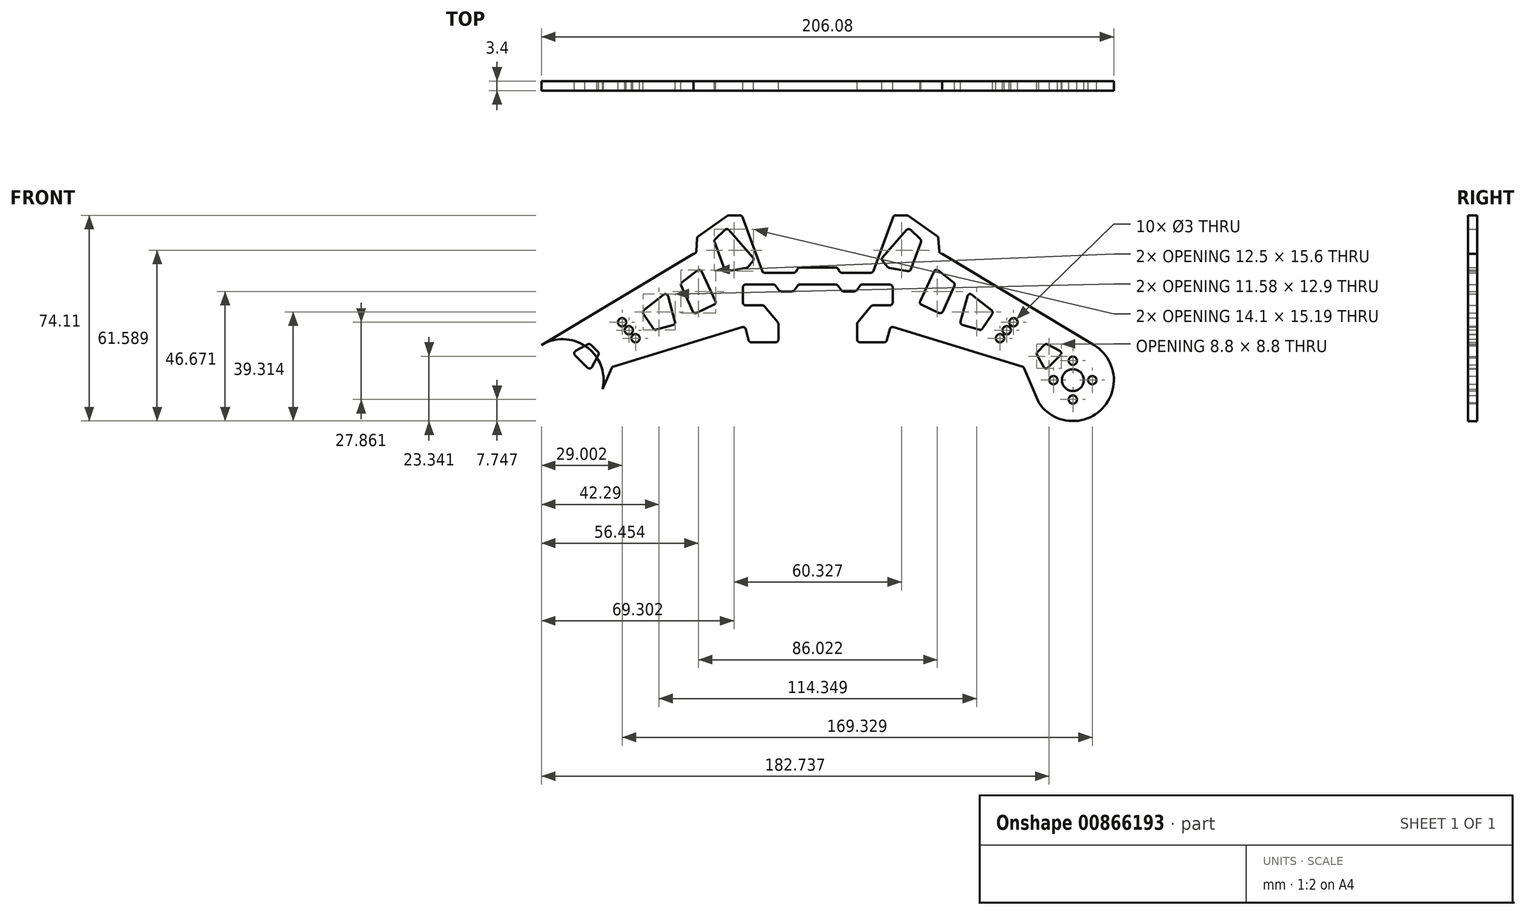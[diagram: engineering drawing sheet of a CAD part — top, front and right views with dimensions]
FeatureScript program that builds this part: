
annotation { "Feature Type Name" : "Feature", "Feature Type Description" : "" }
export const myFeature = defineFeature(function(context is Context, id is Id, definition is map)
    precondition{}
    {
        {
            var Q0;
            Q0=qCreatedBy(makeId("Front.planeOp"),FACE);
            var sketch = newSketch(context, id + "F0", { "sketchPlane" : qUnion([Q0])});
            skLineSegment(sketch, "E0", {"start": v(-61.8, 49.47) * mm, "end": v(-7.12, 16.59) * mm});
            skCircle(sketch, "E1", {"center": v(-14.72, 3.95) * mm, "radius": 14.75 * mm});
            skLineSegment(sketch, "E2", {"start": v(-32.97, 8.88) * mm, "end": v(-79.35, 23.06) * mm});
            skLineSegment(sketch, "E3", {"start": v(-62.84, 50.4) * mm, "end": v(-63.17, 55.1) * mm});
            skLineSegment(sketch, "E4", {"start": v(-63.6, 55.84) * mm, "end": v(-74, 63.13) * mm});
            skLineSegment(sketch, "E5", {"start": v(-74.58, 63.31) * mm, "end": v(-78.56, 63.31) * mm});
            skLineSegment(sketch, "E6", {"start": v(-79.5, 62.65) * mm, "end": v(-86.55, 43.3) * mm});
            skLineSegment(sketch, "E7", {"start": v(-87.49, 42.64) * mm, "end": v(-97.91, 42.64) * mm});
            skLineSegment(sketch, "E8", {"start": v(-98.78, 43.14) * mm, "end": v(-99.3, 44.04) * mm});
            skLineSegment(sketch, "E9", {"start": v(-100.16, 44.54) * mm, "end": v(-106.59, 44.54) * mm});
            skLineSegment(sketch, "E10", {"start": v(-80.6, 22.36) * mm, "end": v(-81.7, 18.31) * mm});
            skLineSegment(sketch, "E11", {"start": v(-82.66, 17.57) * mm, "end": v(-91.4, 17.57) * mm});
            skLineSegment(sketch, "E12", {"start": v(-92.4, 18.57) * mm, "end": v(-92.4, 24.2) * mm});
            skLineSegment(sketch, "E13", {"start": v(-92.16, 24.85) * mm, "end": v(-87.39, 30.53) * mm});
            skLineSegment(sketch, "E14", {"start": v(-86.62, 30.89) * mm, "end": v(-80.62, 30.89) * mm});
            skLineSegment(sketch, "E15", {"start": v(-79.62, 31.89) * mm, "end": v(-79.62, 37.39) * mm});
            skLineSegment(sketch, "E16", {"start": v(-80.62, 38.39) * mm, "end": v(-90.62, 38.39) * mm});
            skLineSegment(sketch, "E17", {"start": v(-91.44, 37.96) * mm, "end": v(-92.57, 36.36) * mm});
            skLineSegment(sketch, "E18", {"start": v(-93.39, 35.93) * mm, "end": v(-97.34, 35.93) * mm});
            skLineSegment(sketch, "E19", {"start": v(-98.16, 36.36) * mm, "end": v(-99.29, 37.96) * mm});
            skLineSegment(sketch, "E20", {"start": v(-100.1, 38.39) * mm, "end": v(-106.59, 38.39) * mm});
            skLineSegment(sketch, "E21", {"start": v(-32.34, 8.32) * mm, "end": v(-27.05, -4.14) * mm});
            skCircle(sketch, "E22", {"center": v(-14.72, 3.95) * mm, "radius": 3.93 * mm});
            skLineSegment(sketch, "E23", {"start": v(-14.72, 3.95) * mm, "end": v(-14.72, 10.95) * mm, "construction": true});
            skLineSegment(sketch, "E24", {"start": v(-14.72, 3.95) * mm, "end": v(-7.72, 3.95) * mm, "construction": true});
            skLineSegment(sketch, "E25", {"start": v(-14.72, 3.95) * mm, "end": v(-21.72, 3.95) * mm, "construction": true});
            skLineSegment(sketch, "E26", {"start": v(-14.72, 3.95) * mm, "end": v(-14.72, -3.05) * mm, "construction": true});
            skCircle(sketch, "E27", {"center": v(-14.72, -3.05) * mm, "radius": 1.5 * mm});
            skCircle(sketch, "E28", {"center": v(-7.72, 3.95) * mm, "radius": 1.5 * mm});
            skCircle(sketch, "E29", {"center": v(-14.72, 10.95) * mm, "radius": 1.5 * mm});
            skCircle(sketch, "E30", {"center": v(-21.72, 3.95) * mm, "radius": 1.5 * mm});
            skLineSegment(sketch, "E31", {"start": v(-23.67, 8.43) * mm, "end": v(-19.2, 12.9) * mm});
            skLineSegment(sketch, "E32", {"start": v(-19.43, 14.48) * mm, "end": v(-23.76, 16.82) * mm});
            skLineSegment(sketch, "E33", {"start": v(-24.94, 16.65) * mm, "end": v(-27.42, 14.17) * mm});
            skLineSegment(sketch, "E34", {"start": v(-27.6, 12.98) * mm, "end": v(-25.26, 8.66) * mm});
            skPoint(sketch, "E35", {"position": v(-21.44, 10.66) * mm});
            skCircle(sketch, "E36", {"center": v(-40.97, 19.03) * mm, "radius": 1.5 * mm});
            skCircle(sketch, "E37", {"center": v(-38.55, 21.92) * mm, "radius": 1.5 * mm});
            skCircle(sketch, "E38", {"center": v(-36.12, 24.8) * mm, "radius": 1.5 * mm});
            skLineSegment(sketch, "E39", {"start": v(-38.55, 21.92) * mm, "end": v(-40.97, 19.03) * mm, "construction": true});
            skLineSegment(sketch, "E40", {"start": v(-36.12, 24.8) * mm, "end": v(-38.55, 21.92) * mm, "construction": true});
            skLineSegment(sketch, "E41", {"start": v(-47.33, 22.5) * mm, "end": v(-43.8, 27.78) * mm});
            skLineSegment(sketch, "E42", {"start": v(-44, 29.12) * mm, "end": v(-51.1, 34.75) * mm});
            skLineSegment(sketch, "E43", {"start": v(-52.69, 34.23) * mm, "end": v(-55.17, 25.06) * mm});
            skLineSegment(sketch, "E44", {"start": v(-54.48, 23.84) * mm, "end": v(-48.43, 22.1) * mm});
            skPoint(sketch, "E45", {"position": v(-45.5, 25.23) * mm});
            skPoint(sketch, "E46.endSnap0", {"position": v(-56.43, 16.06) * mm});
            skLineSegment(sketch, "E47", {"start": v(-62.92, 28.16) * mm, "end": v(-69.25, 31.12) * mm});
            skLineSegment(sketch, "E48", {"start": v(-69.73, 32.45) * mm, "end": v(-64.77, 43.1) * mm});
            skLineSegment(sketch, "E49", {"start": v(-63.25, 43.46) * mm, "end": v(-57.7, 39.17) * mm});
            skLineSegment(sketch, "E50", {"start": v(-57.41, 37.97) * mm, "end": v(-61.58, 28.66) * mm});
            skPoint(sketch, "E51.visualSharp", {"position": v(-64.24, 44.23) * mm});
            skArc(sketch, "E51.filletArc", {"start": v(-63.25, 43.46) * mm, "mid": v(-64.1, 43.64) * mm, "end": v(-64.77, 43.1) * mm});
            skPoint(sketch, "E52.visualSharp", {"position": v(-57.09, 38.69) * mm});
            skArc(sketch, "E52.filletArc", {"start": v(-57.41, 37.97) * mm, "mid": v(-57.35, 38.62) * mm, "end": v(-57.7, 39.17) * mm});
            skPoint(sketch, "E53.visualSharp", {"position": v(-70.15, 31.54) * mm});
            skArc(sketch, "E53.filletArc", {"start": v(-69.73, 32.45) * mm, "mid": v(-69.76, 31.68) * mm, "end": v(-69.25, 31.12) * mm});
            skPoint(sketch, "E54.visualSharp", {"position": v(-62, 27.74) * mm});
            skArc(sketch, "E54.filletArc", {"start": v(-62.92, 28.16) * mm, "mid": v(-62.14, 28.13) * mm, "end": v(-61.58, 28.66) * mm});
            skPoint(sketch, "E55.visualSharp", {"position": v(-52.29, 35.7) * mm});
            skArc(sketch, "E55.filletArc", {"start": v(-51.1, 34.75) * mm, "mid": v(-52.03, 34.91) * mm, "end": v(-52.69, 34.23) * mm});
            skPoint(sketch, "E56.visualSharp", {"position": v(-43.28, 28.55) * mm});
            skArc(sketch, "E56.filletArc", {"start": v(-43.8, 27.78) * mm, "mid": v(-43.63, 28.5) * mm, "end": v(-44, 29.12) * mm});
            skPoint(sketch, "E57.visualSharp", {"position": v(-55.42, 24.1) * mm});
            skArc(sketch, "E57.filletArc", {"start": v(-55.17, 25.06) * mm, "mid": v(-55.07, 24.3) * mm, "end": v(-54.48, 23.84) * mm});
            skPoint(sketch, "E58.visualSharp", {"position": v(-47.73, 21.9) * mm});
            skArc(sketch, "E58.filletArc", {"start": v(-48.43, 22.1) * mm, "mid": v(-47.81, 22.13) * mm, "end": v(-47.33, 22.5) * mm});
            skPoint(sketch, "E59.visualSharp", {"position": v(-27.95, 13.64) * mm});
            skArc(sketch, "E59.filletArc", {"start": v(-27.42, 14.17) * mm, "mid": v(-27.7, 13.6) * mm, "end": v(-27.6, 12.98) * mm});
            skPoint(sketch, "E60.visualSharp", {"position": v(-24.41, 17.18) * mm});
            skArc(sketch, "E60.filletArc", {"start": v(-23.76, 16.82) * mm, "mid": v(-24.38, 16.93) * mm, "end": v(-24.94, 16.65) * mm});
            skPoint(sketch, "E61.visualSharp", {"position": v(-24.62, 7.48) * mm});
            skArc(sketch, "E61.filletArc", {"start": v(-25.26, 8.66) * mm, "mid": v(-24.52, 8.15) * mm, "end": v(-23.67, 8.43) * mm});
            skPoint(sketch, "E62.visualSharp", {"position": v(-18.25, 13.85) * mm});
            skArc(sketch, "E62.filletArc", {"start": v(-19.2, 12.9) * mm, "mid": v(-18.92, 13.75) * mm, "end": v(-19.43, 14.48) * mm});
            skPoint(sketch, "E63.visualSharp", {"position": v(-62.82, 50.08) * mm});
            skArc(sketch, "E63.filletArc", {"start": v(-62.84, 50.4) * mm, "mid": v(-62.51, 49.72) * mm, "end": v(-61.8, 49.47) * mm});
            skPoint(sketch, "E64.visualSharp", {"position": v(-63.2, 55.57) * mm});
            skArc(sketch, "E64.filletArc", {"start": v(-63.17, 55.1) * mm, "mid": v(-63.3, 55.52) * mm, "end": v(-63.6, 55.84) * mm});
            skPoint(sketch, "E65.visualSharp", {"position": v(-99.59, 38.39) * mm});
            skArc(sketch, "E65.filletArc", {"start": v(-99.29, 37.96) * mm, "mid": v(-99.64, 38.28) * mm, "end": v(-100.1, 38.39) * mm});
            skPoint(sketch, "E66.visualSharp", {"position": v(-97.86, 35.93) * mm});
            skArc(sketch, "E66.filletArc", {"start": v(-98.16, 36.36) * mm, "mid": v(-97.8, 36.04) * mm, "end": v(-97.34, 35.93) * mm});
            skPoint(sketch, "E67.visualSharp", {"position": v(-92.86, 35.93) * mm});
            skArc(sketch, "E67.filletArc", {"start": v(-93.39, 35.93) * mm, "mid": v(-92.92, 36.04) * mm, "end": v(-92.57, 36.36) * mm});
            skPoint(sketch, "E68.visualSharp", {"position": v(-91.14, 38.39) * mm});
            skArc(sketch, "E68.filletArc", {"start": v(-90.62, 38.39) * mm, "mid": v(-91.08, 38.28) * mm, "end": v(-91.44, 37.96) * mm});
            skPoint(sketch, "E69.visualSharp", {"position": v(-79.62, 38.39) * mm});
            skArc(sketch, "E69.filletArc", {"start": v(-79.62, 37.39) * mm, "mid": v(-79.92, 38.1) * mm, "end": v(-80.62, 38.39) * mm});
            skPoint(sketch, "E70.visualSharp", {"position": v(-79.62, 30.89) * mm});
            skArc(sketch, "E70.filletArc", {"start": v(-80.62, 30.89) * mm, "mid": v(-79.92, 31.18) * mm, "end": v(-79.62, 31.89) * mm});
            skPoint(sketch, "E71.visualSharp", {"position": v(-87.09, 30.89) * mm});
            skArc(sketch, "E71.filletArc", {"start": v(-86.62, 30.89) * mm, "mid": v(-87.05, 30.8) * mm, "end": v(-87.39, 30.53) * mm});
            skPoint(sketch, "E72.visualSharp", {"position": v(-92.4, 24.57) * mm});
            skArc(sketch, "E72.filletArc", {"start": v(-92.16, 24.85) * mm, "mid": v(-92.33, 24.55) * mm, "end": v(-92.4, 24.2) * mm});
            skPoint(sketch, "E73.visualSharp", {"position": v(-92.4, 17.57) * mm});
            skArc(sketch, "E73.filletArc", {"start": v(-92.4, 18.57) * mm, "mid": v(-92.1, 17.86) * mm, "end": v(-91.4, 17.57) * mm});
            skPoint(sketch, "E74.visualSharp", {"position": v(-81.9, 17.57) * mm});
            skArc(sketch, "E74.filletArc", {"start": v(-82.66, 17.57) * mm, "mid": v(-82.05, 17.78) * mm, "end": v(-81.7, 18.31) * mm});
            skPoint(sketch, "E75.visualSharp", {"position": v(-80.34, 23.37) * mm});
            skArc(sketch, "E75.filletArc", {"start": v(-79.35, 23.06) * mm, "mid": v(-80.13, 22.98) * mm, "end": v(-80.6, 22.36) * mm});
            skPoint(sketch, "E76.visualSharp", {"position": v(-86.79, 42.64) * mm});
            skArc(sketch, "E76.filletArc", {"start": v(-87.49, 42.64) * mm, "mid": v(-86.91, 42.82) * mm, "end": v(-86.55, 43.3) * mm});
            skPoint(sketch, "E77.visualSharp", {"position": v(-32.52, 8.75) * mm});
            skArc(sketch, "E77.filletArc", {"start": v(-32.34, 8.32) * mm, "mid": v(-32.6, 8.67) * mm, "end": v(-32.97, 8.88) * mm});
            skPoint(sketch, "E78.visualSharp", {"position": v(-79.26, 63.31) * mm});
            skArc(sketch, "E78.filletArc", {"start": v(-78.56, 63.31) * mm, "mid": v(-79.14, 63.13) * mm, "end": v(-79.5, 62.65) * mm});
            skPoint(sketch, "E79.visualSharp", {"position": v(-74.26, 63.31) * mm});
            skArc(sketch, "E79.filletArc", {"start": v(-74, 63.13) * mm, "mid": v(-74.28, 63.27) * mm, "end": v(-74.58, 63.31) * mm});
            skLineSegment(sketch, "E80.MirrorCS", {"start": v(-74.58, 58.04) * mm, "end": v(-83.22, 48.2) * mm});
            skLineSegment(sketch, "E81.MirrorCS", {"start": v(-69.68, 54.77) * mm, "end": v(-73.13, 58.1) * mm});
            skLineSegment(sketch, "E82.MirrorCS", {"start": v(-80.87, 44.42) * mm, "end": v(-74.18, 43.21) * mm});
            skLineSegment(sketch, "E83.MirrorCS", {"start": v(-73.07, 43.85) * mm, "end": v(-69.43, 53.7) * mm});
            skLineSegment(sketch, "E84.MirrorCS", {"start": v(-83.24, 46.9) * mm, "end": v(-81.46, 44.77) * mm});
            skPoint(sketch, "E85.MirrorP", {"position": v(-86.1, 45.52) * mm});
            skPoint(sketch, "E86.visualSharp", {"position": v(-73.89, 58.83) * mm});
            skArc(sketch, "E86.filletArc", {"start": v(-73.13, 58.1) * mm, "mid": v(-73.87, 58.38) * mm, "end": v(-74.58, 58.04) * mm});
            skPoint(sketch, "E87.visualSharp", {"position": v(-69.2, 54.32) * mm});
            skArc(sketch, "E87.filletArc", {"start": v(-69.43, 53.7) * mm, "mid": v(-69.4, 54.28) * mm, "end": v(-69.68, 54.77) * mm});
            skPoint(sketch, "E88.visualSharp", {"position": v(-73.36, 43.06) * mm});
            skArc(sketch, "E88.filletArc", {"start": v(-74.18, 43.21) * mm, "mid": v(-73.5, 43.33) * mm, "end": v(-73.07, 43.85) * mm});
            skPoint(sketch, "E89.visualSharp", {"position": v(-81.23, 44.49) * mm});
            skArc(sketch, "E89.filletArc", {"start": v(-81.46, 44.77) * mm, "mid": v(-81.2, 44.54) * mm, "end": v(-80.87, 44.42) * mm});
            skPoint(sketch, "E90.visualSharp", {"position": v(-83.79, 47.56) * mm});
            skArc(sketch, "E90.filletArc", {"start": v(-83.22, 48.2) * mm, "mid": v(-83.47, 47.56) * mm, "end": v(-83.24, 46.9) * mm});
            skLineSegment(sketch, "E91", {"start": v(-36.12, 24.8) * mm, "end": v(-30.98, 30.94) * mm, "construction": true});
            skLineSegment(sketch, "E92", {"start": v(-40.97, 19.03) * mm, "end": v(-46.11, 12.9) * mm, "construction": true});
            skLineSegment(sketch, "E93", {"start": v(-14.72, 3.95) * mm, "end": v(-21.44, 10.66) * mm, "construction": true});
            skLineSegment(sketch, "E94", {"start": v(-47.73, 21.9) * mm, "end": v(-52.47, 14.84) * mm, "construction": true});
            skPoint(sketch, "E95.endSnap0", {"position": v(-34.46, 33.03) * mm});
            skLineSegment(sketch, "E96", {"start": v(-64.92, 29.1) * mm, "end": v(-68.24, 19.66) * mm, "construction": true});
            skLineSegment(sketch, "E97", {"start": v(-55.42, 24.1) * mm, "end": v(-57.6, 16.06) * mm, "construction": true});
            skLineSegment(sketch, "E98", {"start": v(-43.28, 28.55) * mm, "end": v(-38.6, 35.52) * mm, "construction": true});
            skLineSegment(sketch, "E99", {"start": v(-52.29, 35.7) * mm, "end": v(-50.41, 42.62) * mm, "construction": true});
            skPoint(sketch, "E100.visualSharp", {"position": v(-99.59, 44.54) * mm});
            skArc(sketch, "E100.filletArc", {"start": v(-99.3, 44.04) * mm, "mid": v(-99.66, 44.4) * mm, "end": v(-100.16, 44.54) * mm});
            skPoint(sketch, "E101.visualSharp", {"position": v(-98.49, 42.64) * mm});
            skArc(sketch, "E101.filletArc", {"start": v(-98.78, 43.14) * mm, "mid": v(-98.41, 42.77) * mm, "end": v(-97.91, 42.64) * mm});
            skLineSegment(sketch, "E102", {"start": v(-106.59, 44.54) * mm, "end": v(-106.59, 38.39) * mm, "construction": true});
            skArc(sketch, "E103.MirrorCS", {"start": v(-119.79, 35.93) * mm, "mid": v(-120.25, 36.04) * mm, "end": v(-120.6, 36.36) * mm});
            skArc(sketch, "E104.MirrorCS", {"start": v(-115, 36.36) * mm, "mid": v(-115.36, 36.04) * mm, "end": v(-115.83, 35.93) * mm});
            skLineSegment(sketch, "E105.MirrorCS", {"start": v(-121.73, 37.96) * mm, "end": v(-120.6, 36.36) * mm});
            skArc(sketch, "E106.MirrorCS", {"start": v(-122.55, 38.39) * mm, "mid": v(-122.09, 38.28) * mm, "end": v(-121.73, 37.96) * mm});
            skLineSegment(sketch, "E107.MirrorCS", {"start": v(-119.79, 35.93) * mm, "end": v(-115.83, 35.93) * mm});
            skArc(sketch, "E108.MirrorCS", {"start": v(-113.88, 37.96) * mm, "mid": v(-113.53, 38.28) * mm, "end": v(-113.06, 38.39) * mm});
            skLineSegment(sketch, "E109.MirrorCS", {"start": v(-115, 36.36) * mm, "end": v(-113.88, 37.96) * mm});
            skArc(sketch, "E110.MirrorCS", {"start": v(-131.7, 44.77) * mm, "mid": v(-131.97, 44.54) * mm, "end": v(-132.3, 44.42) * mm});
            skArc(sketch, "E111.MirrorCS", {"start": v(-180.83, 8.32) * mm, "mid": v(-180.58, 8.67) * mm, "end": v(-180.2, 8.88) * mm});
            skArc(sketch, "E112.MirrorCS", {"start": v(-113.87, 44.04) * mm, "mid": v(-113.5, 44.4) * mm, "end": v(-113, 44.54) * mm});
            skArc(sketch, "E113.MirrorCS", {"start": v(-164.74, 22.1) * mm, "mid": v(-165.36, 22.13) * mm, "end": v(-165.84, 22.5) * mm});
            skLineSegment(sketch, "E114.MirrorCS", {"start": v(-114.4, 43.14) * mm, "end": v(-113.87, 44.04) * mm});
            skArc(sketch, "E115.MirrorCS", {"start": v(-114.4, 43.14) * mm, "mid": v(-114.76, 42.77) * mm, "end": v(-115.26, 42.64) * mm});
            skArc(sketch, "E116.MirrorCS", {"start": v(-150.33, 50.4) * mm, "mid": v(-150.66, 49.72) * mm, "end": v(-151.37, 49.47) * mm});
            skArc(sketch, "E117.MirrorCS", {"start": v(-133.82, 23.06) * mm, "mid": v(-133.04, 22.98) * mm, "end": v(-132.56, 22.36) * mm});
            skArc(sketch, "E118.MirrorCS", {"start": v(-129.95, 48.2) * mm, "mid": v(-129.7, 47.56) * mm, "end": v(-129.93, 46.9) * mm});
            skArc(sketch, "E119.MirrorCS", {"start": v(-132.55, 30.89) * mm, "mid": v(-133.25, 31.18) * mm, "end": v(-133.55, 31.89) * mm});
            skArc(sketch, "E120.MirrorCS", {"start": v(-120.78, 18.57) * mm, "mid": v(-121.07, 17.86) * mm, "end": v(-121.78, 17.57) * mm});
            skLineSegment(sketch, "E121.MirrorCS", {"start": v(-129.93, 46.9) * mm, "end": v(-131.7, 44.77) * mm});
            skArc(sketch, "E122.MirrorCS", {"start": v(-149.92, 43.46) * mm, "mid": v(-149.08, 43.64) * mm, "end": v(-148.4, 43.1) * mm});
            skArc(sketch, "E123.MirrorCS", {"start": v(-133.55, 37.39) * mm, "mid": v(-133.25, 38.1) * mm, "end": v(-132.55, 38.39) * mm});
            skArc(sketch, "E124.MirrorCS", {"start": v(-121.01, 24.85) * mm, "mid": v(-120.84, 24.55) * mm, "end": v(-120.78, 24.2) * mm});
            skArc(sketch, "E125.MirrorCS", {"start": v(-143.74, 53.7) * mm, "mid": v(-143.78, 54.28) * mm, "end": v(-143.5, 54.77) * mm});
            skArc(sketch, "E126.MirrorCS", {"start": v(-126.55, 30.89) * mm, "mid": v(-126.12, 30.8) * mm, "end": v(-125.78, 30.53) * mm});
            skLineSegment(sketch, "E127.MirrorCS", {"start": v(-150.33, 50.4) * mm, "end": v(-150, 55.1) * mm});
            skLineSegment(sketch, "E128.MirrorCS", {"start": v(-133.55, 31.89) * mm, "end": v(-133.55, 37.39) * mm});
            skLineSegment(sketch, "E129.MirrorCS", {"start": v(-143.5, 54.77) * mm, "end": v(-140.04, 58.1) * mm});
            skArc(sketch, "E130.MirrorCS", {"start": v(-150, 55.1) * mm, "mid": v(-149.87, 55.52) * mm, "end": v(-149.57, 55.84) * mm});
            skArc(sketch, "E131.MirrorCS", {"start": v(-125.68, 42.64) * mm, "mid": v(-126.26, 42.82) * mm, "end": v(-126.62, 43.3) * mm});
            skLineSegment(sketch, "E132.MirrorCS", {"start": v(-120.78, 18.57) * mm, "end": v(-120.78, 24.2) * mm});
            skLineSegment(sketch, "E133.MirrorCS", {"start": v(-165.84, 22.5) * mm, "end": v(-169.38, 27.78) * mm});
            skArc(sketch, "E134.MirrorCS", {"start": v(-134.6, 63.31) * mm, "mid": v(-134.03, 63.13) * mm, "end": v(-133.67, 62.65) * mm});
            skLineSegment(sketch, "E135.MirrorCS", {"start": v(-138.6, 63.31) * mm, "end": v(-134.6, 63.31) * mm});
            skLineSegment(sketch, "E136.MirrorCS", {"start": v(-121.01, 24.85) * mm, "end": v(-125.78, 30.53) * mm});
            skLineSegment(sketch, "E137.MirrorCS", {"start": v(-132.3, 44.42) * mm, "end": v(-138.99, 43.21) * mm});
            skLineSegment(sketch, "E138.MirrorCS", {"start": v(-126.55, 30.89) * mm, "end": v(-132.55, 30.89) * mm});
            skArc(sketch, "E139.MirrorCS", {"start": v(-139.17, 63.13) * mm, "mid": v(-138.9, 63.27) * mm, "end": v(-138.6, 63.31) * mm});
            skArc(sketch, "E140.MirrorCS", {"start": v(-140.04, 58.1) * mm, "mid": v(-139.3, 58.38) * mm, "end": v(-138.6, 58.04) * mm});
            skArc(sketch, "E141.MirrorCS", {"start": v(-138.99, 43.21) * mm, "mid": v(-139.66, 43.33) * mm, "end": v(-140.1, 43.85) * mm});
            skArc(sketch, "E142.MirrorCS", {"start": v(-169.38, 27.78) * mm, "mid": v(-169.54, 28.5) * mm, "end": v(-169.17, 29.12) * mm});
            skLineSegment(sketch, "E143.MirrorCS", {"start": v(-158.7, 23.84) * mm, "end": v(-164.74, 22.1) * mm});
            skLineSegment(sketch, "E144.MirrorCS", {"start": v(-149.92, 43.46) * mm, "end": v(-155.46, 39.17) * mm});
            skArc(sketch, "E145.MirrorCS", {"start": v(-158, 25.06) * mm, "mid": v(-158.1, 24.3) * mm, "end": v(-158.7, 23.84) * mm});
            skArc(sketch, "E146.MirrorCS", {"start": v(-162.07, 34.75) * mm, "mid": v(-161.14, 34.91) * mm, "end": v(-160.49, 34.23) * mm});
            skArc(sketch, "E147.MirrorCS", {"start": v(-155.76, 37.97) * mm, "mid": v(-155.82, 38.62) * mm, "end": v(-155.46, 39.17) * mm});
            skArc(sketch, "E148.MirrorCS", {"start": v(-143.44, 32.45) * mm, "mid": v(-143.4, 31.68) * mm, "end": v(-143.92, 31.12) * mm});
            skLineSegment(sketch, "E149.MirrorCS", {"start": v(-188.23, 16.65) * mm, "end": v(-185.75, 14.17) * mm});
            skArc(sketch, "E150.MirrorCS", {"start": v(-130.51, 17.57) * mm, "mid": v(-131.12, 17.78) * mm, "end": v(-131.48, 18.31) * mm});
            skLineSegment(sketch, "E151.MirrorCS", {"start": v(-193.74, 14.48) * mm, "end": v(-189.41, 16.82) * mm});
            skLineSegment(sketch, "E152.MirrorCS", {"start": v(-132.56, 22.36) * mm, "end": v(-131.48, 18.31) * mm});
            skLineSegment(sketch, "E153.MirrorCS", {"start": v(-174.62, 21.92) * mm, "end": v(-172.2, 19.03) * mm, "construction": true});
            skLineSegment(sketch, "E154.MirrorCS", {"start": v(-150.25, 28.16) * mm, "end": v(-143.92, 31.12) * mm});
            skArc(sketch, "E155.MirrorCS", {"start": v(-187.91, 8.66) * mm, "mid": v(-188.65, 8.15) * mm, "end": v(-189.5, 8.43) * mm});
            skLineSegment(sketch, "E156.MirrorCS", {"start": v(-169.17, 29.12) * mm, "end": v(-162.07, 34.75) * mm});
            skLineSegment(sketch, "E157.MirrorCS", {"start": v(-185.58, 12.98) * mm, "end": v(-187.91, 8.66) * mm});
            skLineSegment(sketch, "E158.MirrorCS", {"start": v(-177.05, 24.8) * mm, "end": v(-174.62, 21.92) * mm, "construction": true});
            skCircle(sketch, "E159.MirrorC", {"center": v(-177.05, 24.8) * mm, "radius": 1.5 * mm});
            skArc(sketch, "E160.MirrorCS", {"start": v(-189.41, 16.82) * mm, "mid": v(-188.8, 16.93) * mm, "end": v(-188.23, 16.65) * mm});
            skCircle(sketch, "E161.MirrorC", {"center": v(-174.62, 21.92) * mm, "radius": 1.5 * mm});
            skCircle(sketch, "E162.MirrorC", {"center": v(-172.2, 19.03) * mm, "radius": 1.5 * mm});
            skLineSegment(sketch, "E163.MirrorCS", {"start": v(-189.5, 8.43) * mm, "end": v(-193.97, 12.9) * mm});
            skArc(sketch, "E164.MirrorCS", {"start": v(-193.97, 12.9) * mm, "mid": v(-194.25, 13.75) * mm, "end": v(-193.74, 14.48) * mm});
            skArc(sketch, "E165.MirrorCS", {"start": v(-185.75, 14.17) * mm, "mid": v(-185.47, 13.6) * mm, "end": v(-185.58, 12.98) * mm});
            skArc(sketch, "E166.MirrorCS", {"start": v(-150.25, 28.16) * mm, "mid": v(-151.03, 28.13) * mm, "end": v(-151.59, 28.66) * mm});
            skCircle(sketch, "E167.MirrorC", {"center": v(-191.45, 3.95) * mm, "radius": 1.5 * mm});
            skLineSegment(sketch, "E168.MirrorCS", {"start": v(-198.45, 3.95) * mm, "end": v(-191.45, 3.95) * mm, "construction": true});
            skLineSegment(sketch, "E169.MirrorCS", {"start": v(-198.45, 3.95) * mm, "end": v(-191.73, 10.66) * mm, "construction": true});
            skLineSegment(sketch, "E170.MirrorCS", {"start": v(-113, 44.54) * mm, "end": v(-106.59, 44.54) * mm});
            skLineSegment(sketch, "E171.MirrorCS", {"start": v(-198.45, 3.95) * mm, "end": v(-198.45, 10.95) * mm, "construction": true});
            skLineSegment(sketch, "E172.MirrorCS", {"start": v(-113.06, 38.39) * mm, "end": v(-106.59, 38.39) * mm});
            skLineSegment(sketch, "E173.MirrorCS", {"start": v(-149.57, 55.84) * mm, "end": v(-139.17, 63.13) * mm});
            skLineSegment(sketch, "E174.MirrorCS", {"start": v(-198.45, 3.95) * mm, "end": v(-205.45, 3.95) * mm, "construction": true});
            skCircle(sketch, "E175.MirrorC", {"center": v(-198.45, 3.95) * mm, "radius": 3.93 * mm});
            skLineSegment(sketch, "E176.MirrorCS", {"start": v(-198.45, 3.95) * mm, "end": v(-198.45, -3.05) * mm, "construction": true});
            skLineSegment(sketch, "E177.MirrorCS", {"start": v(-157.75, 24.1) * mm, "end": v(-155.57, 16.06) * mm, "construction": true});
            skCircle(sketch, "E178.MirrorC", {"center": v(-198.45, 10.95) * mm, "radius": 1.5 * mm});
            skCircle(sketch, "E179.MirrorC", {"center": v(-198.45, -3.05) * mm, "radius": 1.5 * mm});
            skCircle(sketch, "E180.MirrorC", {"center": v(-205.45, 3.95) * mm, "radius": 1.5 * mm});
            skPoint(sketch, "E181.MirrorP", {"position": v(-139.81, 43.06) * mm});
            skPoint(sketch, "E182.MirrorP", {"position": v(-133.55, 30.89) * mm});
            skLineSegment(sketch, "E183.MirrorCS", {"start": v(-125.68, 42.64) * mm, "end": v(-115.26, 42.64) * mm});
            skPoint(sketch, "E184.MirrorP", {"position": v(-129.38, 47.56) * mm});
            skLineSegment(sketch, "E185.MirrorCS", {"start": v(-155.76, 37.97) * mm, "end": v(-151.59, 28.66) * mm});
            skPoint(sketch, "E186.MirrorP", {"position": v(-114.68, 42.64) * mm});
            skPoint(sketch, "E187.MirrorP", {"position": v(-115.3, 35.93) * mm});
            skLineSegment(sketch, "E188.MirrorCS", {"start": v(-172.2, 19.03) * mm, "end": v(-167.06, 12.9) * mm, "construction": true});
            skLineSegment(sketch, "E189.MirrorCS", {"start": v(-180.83, 8.32) * mm, "end": v(-186.12, -4.14) * mm});
            skLineSegment(sketch, "E190.MirrorCS", {"start": v(-143.44, 32.45) * mm, "end": v(-148.4, 43.1) * mm});
            skPoint(sketch, "E191.MirrorP", {"position": v(-148.93, 44.23) * mm});
            skLineSegment(sketch, "E192.MirrorCS", {"start": v(-180.2, 8.88) * mm, "end": v(-133.82, 23.06) * mm});
            skLineSegment(sketch, "E193.MirrorCS", {"start": v(-138.6, 58.04) * mm, "end": v(-129.95, 48.2) * mm});
            skPoint(sketch, "E194.MirrorP", {"position": v(-150.35, 50.08) * mm});
            skPoint(sketch, "E195.MirrorP", {"position": v(-120.3, 35.93) * mm});
            skPoint(sketch, "E196.MirrorP", {"position": v(-139.28, 58.83) * mm});
            skPoint(sketch, "E197.MirrorP", {"position": v(-165.44, 21.9) * mm});
            skLineSegment(sketch, "E198.MirrorCS", {"start": v(-130.51, 17.57) * mm, "end": v(-121.78, 17.57) * mm});
            skPoint(sketch, "E199.MirrorP", {"position": v(-126.08, 30.89) * mm});
            skLineSegment(sketch, "E200.MirrorCS", {"start": v(-148.25, 29.1) * mm, "end": v(-144.93, 19.66) * mm, "construction": true});
            skPoint(sketch, "E201.MirrorP", {"position": v(-132.83, 23.37) * mm});
            skLineSegment(sketch, "E202.MirrorCS", {"start": v(-169.9, 28.55) * mm, "end": v(-174.57, 35.52) * mm, "construction": true});
            skLineSegment(sketch, "E203.MirrorCS", {"start": v(-165.44, 21.9) * mm, "end": v(-160.7, 14.84) * mm, "construction": true});
            skLineSegment(sketch, "E204.MirrorCS", {"start": v(-140.1, 43.85) * mm, "end": v(-143.74, 53.7) * mm});
            skLineSegment(sketch, "E205.MirrorCS", {"start": v(-160.49, 34.23) * mm, "end": v(-158, 25.06) * mm});
            skPoint(sketch, "E206.MirrorP", {"position": v(-143.97, 54.32) * mm});
            skLineSegment(sketch, "E207.MirrorCS", {"start": v(-160.88, 35.7) * mm, "end": v(-162.76, 42.62) * mm, "construction": true});
            skLineSegment(sketch, "E208.MirrorCS", {"start": v(-177.05, 24.8) * mm, "end": v(-182.19, 30.94) * mm, "construction": true});
            skLineSegment(sketch, "E209.MirrorCS", {"start": v(-133.67, 62.65) * mm, "end": v(-126.62, 43.3) * mm});
            skPoint(sketch, "E210.MirrorP", {"position": v(-133.55, 38.39) * mm});
            skPoint(sketch, "E211.MirrorP", {"position": v(-113.59, 38.39) * mm});
            skPoint(sketch, "E212.MirrorP", {"position": v(-126.38, 42.64) * mm});
            skLineSegment(sketch, "E213.MirrorCS", {"start": v(-132.55, 38.39) * mm, "end": v(-122.55, 38.39) * mm});
            skPoint(sketch, "E214.MirrorP", {"position": v(-149.97, 55.57) * mm});
            skPoint(sketch, "E215.MirrorP", {"position": v(-143.02, 31.54) * mm});
            skPoint(sketch, "E216.MirrorP", {"position": v(-157.75, 24.1) * mm});
            skPoint(sketch, "E217.MirrorP", {"position": v(-180.65, 8.75) * mm});
            skPoint(sketch, "E218.MirrorP", {"position": v(-160.88, 35.7) * mm});
            skPoint(sketch, "E219.MirrorP", {"position": v(-127.07, 45.52) * mm});
            skPoint(sketch, "E220.MirrorP", {"position": v(-133.9, 63.31) * mm});
            skPoint(sketch, "E221.MirrorP", {"position": v(-188.55, 7.48) * mm});
            skPoint(sketch, "E222.MirrorP", {"position": v(-151.17, 27.74) * mm});
            skPoint(sketch, "E223.MirrorP", {"position": v(-138.9, 63.31) * mm});
            skPoint(sketch, "E224.MirrorP", {"position": v(-156.74, 16.06) * mm});
            skPoint(sketch, "E225.MirrorP", {"position": v(-113.59, 44.54) * mm});
            skPoint(sketch, "E226.MirrorP", {"position": v(-131.28, 17.57) * mm});
            skPoint(sketch, "E227.MirrorP", {"position": v(-131.94, 44.49) * mm});
            skPoint(sketch, "E228.MirrorP", {"position": v(-178.71, 33.03) * mm});
            skPoint(sketch, "E229.MirrorP", {"position": v(-120.78, 17.57) * mm});
            skPoint(sketch, "E230.MirrorP", {"position": v(-156.08, 38.69) * mm});
            skLineSegment(sketch, "E231.MirrorCS", {"start": v(-151.37, 49.47) * mm, "end": v(-206.05, 16.59) * mm});
            skPoint(sketch, "E232.MirrorP", {"position": v(-191.73, 10.66) * mm});
            skPoint(sketch, "E233.MirrorP", {"position": v(-120.78, 24.57) * mm});
            skCircle(sketch, "E234.MirrorC", {"center": v(-198.45, 3.95) * mm, "radius": 14.75 * mm});
            skPoint(sketch, "E235.MirrorP", {"position": v(-194.92, 13.85) * mm});
            skPoint(sketch, "E236.MirrorP", {"position": v(-169.9, 28.55) * mm});
            skPoint(sketch, "E237.MirrorP", {"position": v(-185.22, 13.64) * mm});
            skPoint(sketch, "E238.MirrorP", {"position": v(-188.76, 17.18) * mm});
            skPoint(sketch, "E239.MirrorP", {"position": v(-122.03, 38.39) * mm});
            skPoint(sketch, "E240.MirrorP", {"position": v(-167.66, 25.23) * mm});
            skSolve(sketch);
        }
        {
            var Q0;
            {var subQ6=sQuery(id+"F0.wireOp",EDGE,"E0");Q0=makeQuery(id+"F0.imprint","IMPRINT",FACE,{"disambiguationData":[TD([[makeQuery(id+"F0.imprint","IMPRINT",EDGE,{"derivedFrom":subQ6}),-1.0]])]});}
            var Q1;
            Q1=makeQuery(id+"F0.imprint","IMPRINT",FACE,{"disambiguationData":[TD([[makeQuery(id+"F0.imprint","IMPRINT",EDGE,{"derivedFrom":sQuery(id+"F0.wireOp",EDGE,"E22")}),-1.0]])]});
            var Q2;
            Q2=makeQuery(id+"F0.imprint","IMPRINT",FACE,{"disambiguationData":[TD([[makeQuery(id+"F0.imprint","IMPRINT",EDGE,{"derivedFrom":sQuery(id+"F0.wireOp",EDGE,"E2")}),-1.0]])]});
            var Q3;
            Q3=makeQuery(id+"F0.imprint","IMPRINT",FACE,{"disambiguationData":[TD([[makeQuery(id+"F0.imprint","IMPRINT",EDGE,{"derivedFrom":sQuery(id+"F0.wireOp",EDGE,"GO7SgaGN-14ix-WvzC-RXo5-p7i4nn4guVte")}),-1.0]])]});
            var Q4;
            {var subQ10=sQuery(id+"F0.wireOp",EDGE,"03afe3cf-b3bd-4cc6-bd7e-a664cd314d599.MirrorCS");Q4=makeQuery(id+"F0.imprint","IMPRINT",FACE,{"disambiguationData":[TD([[makeQuery(id+"F0.imprint","IMPRINT",EDGE,{"derivedFrom":subQ10}),1.0]])]});}
            var Q5;
            Q5=makeQuery(id+"F0.imprint","IMPRINT",FACE,{"disambiguationData":[TD([[makeQuery(id+"F0.imprint","IMPRINT",EDGE,{"derivedFrom":sQuery(id+"F0.wireOp",EDGE,"f801139a-c209-44e9-9f15-a7cc4f0bf8191.MirrorC")}),1.0]])]});
            var Q6;
            {var subQ4=sQuery(id+"F0.wireOp",EDGE,"ae15d4e7-f111-41e7-946d-b25b0354ecab27.MirrorCS");Q6=makeQuery(id+"F0.imprint","IMPRINT",FACE,{"disambiguationData":[TD([[makeQuery(id+"F0.imprint","IMPRINT",EDGE,{"derivedFrom":subQ4}),1.0]])]});}
            var Q7;
            {var subQ8=sQuery(id+"F0.wireOp",EDGE,"E155.MirrorCS");Q7=makeQuery(id+"F0.imprint","IMPRINT",FACE,{"disambiguationData":[TD([[makeQuery(id+"F0.imprint","IMPRINT",EDGE,{"derivedFrom":subQ8}),1.0]])]});}
            extrude(context, id + "F1", {"entities" : qUnion([Q0, Q1, Q2, Q3, Q4, Q5, Q6, Q7]), "depth" : 3.4 * mm, "offsetDistance" : 25 * mm});
        }
    });
